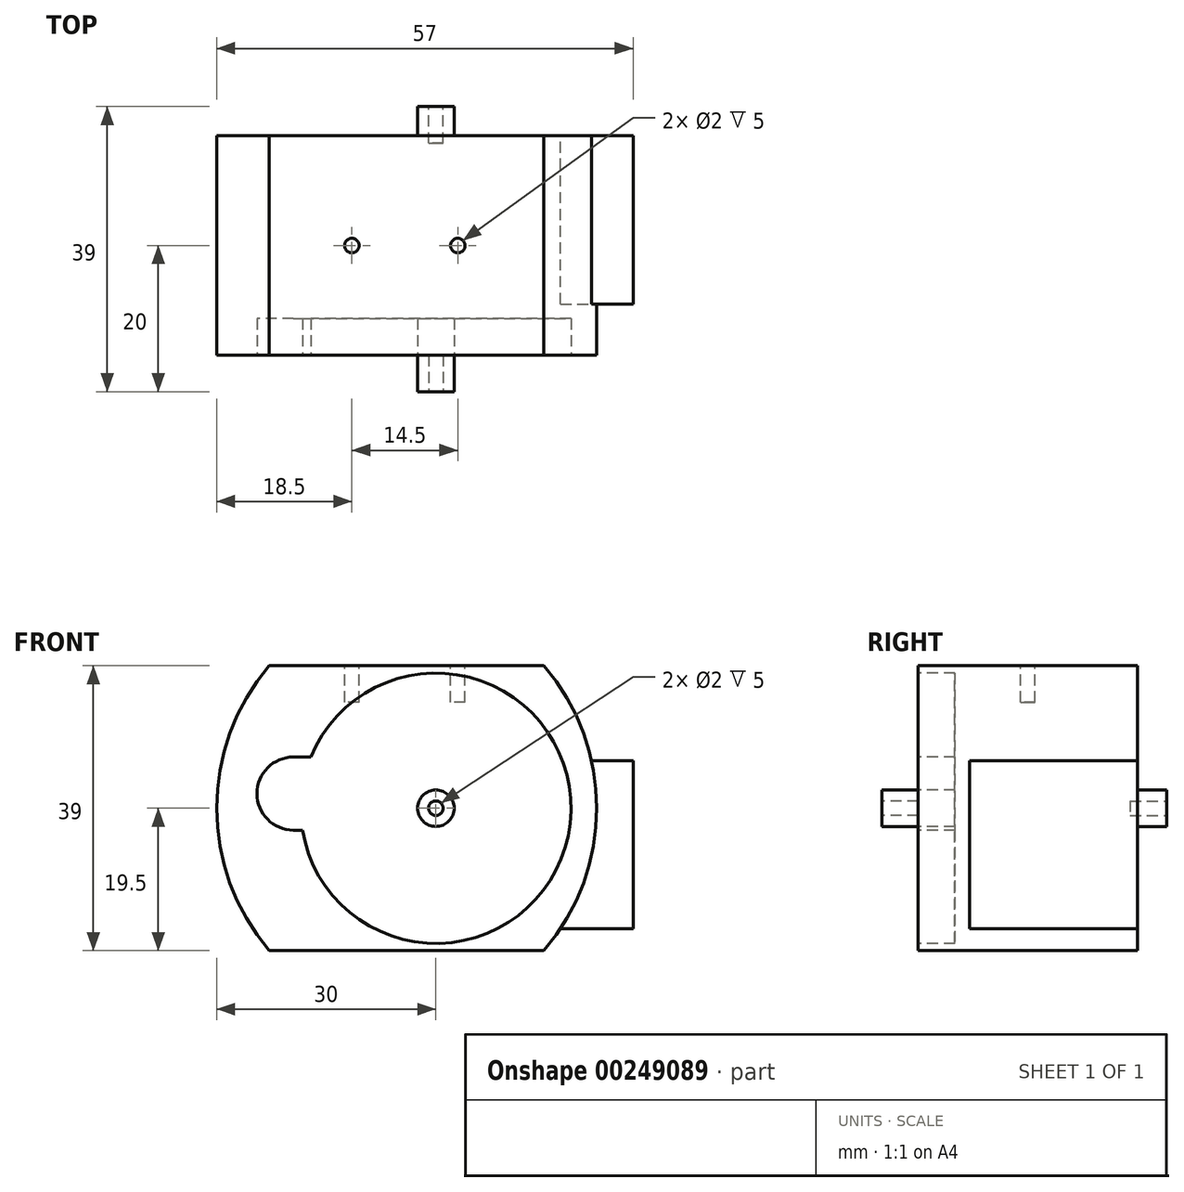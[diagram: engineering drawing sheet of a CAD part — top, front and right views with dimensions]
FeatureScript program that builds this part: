
annotation { "Feature Type Name" : "Feature", "Feature Type Description" : "" }
export const myFeature = defineFeature(function(context is Context, id is Id, definition is map)
    precondition{}
    {
        {
            var Q0;
            Q0=qCreatedBy(makeId("Front.planeOp"),FACE);
            var sketch = newSketch(context, id + "F0", { "sketchPlane" : qUnion([Q0])});
            skLineSegment(sketch, "E0.bottom", {"start": v(-22.8, 19.5) * mm, "end": v(14.8, 19.5) * mm});
            skLineSegment(sketch, "E0.top", {"start": v(-22.8, -19.5) * mm, "end": v(14.8, -19.5) * mm});
            skLineSegment(sketch, "E0.left", {"start": v(-30, 19.5) * mm, "end": v(-30, -19.5) * mm, "construction": true});
            skLineSegment(sketch, "E0.right", {"start": v(22, 19.5) * mm, "end": v(22, -19.5) * mm, "construction": true});
            skArc(sketch, "E1", {"start": v(-22.8, 19.5) * mm, "mid": v(-30, 0) * mm, "end": v(-22.8, -19.5) * mm});
            skArc(sketch, "E2", {"start": v(14.8, -19.5) * mm, "mid": v(22, 0) * mm, "end": v(14.8, 19.5) * mm});
            skCircle(sketch, "E3", {"center": v(0, 0) * mm, "radius": 18.5 * mm});
            skCircle(sketch, "E4", {"center": v(-19.5, 2) * mm, "radius": 5 * mm});
            skLineSegment(sketch, "E5", {"start": v(-19.5, 7) * mm, "end": v(-17.12, 7) * mm});
            skLineSegment(sketch, "E6", {"start": v(-19.5, -3) * mm, "end": v(-18.26, -3) * mm});
            skCircle(sketch, "E7", {"center": v(0, 0) * mm, "radius": 2.5 * mm});
            skCircle(sketch, "E8", {"center": v(-19.5, 2) * mm, "radius": 4.17 * mm, "construction": true});
            skCircle(sketch, "E9", {"center": v(-11.41, 0) * mm, "radius": 4.17 * mm, "construction": true});
            skSolve(sketch);
        }
        {
            var Q0;
            Q0=makeQuery(id+"F0.imprint","IMPRINT",FACE,{"disambiguationData":[TD([[makeQuery(id+"F0.imprint","IMPRINT",EDGE,{"derivedFrom":sQuery(id+"F0.wireOp",EDGE,"E0.bottom")}),-1.0]])]});
            var Q1;
            {var subQ0=sQuery(id+"F0.wireOp",EDGE,"E3");var subQ1=makeQuery(id+"F0.imprint","INTERSECT",VERTEX,{"derivedFrom":[subQ0,sQuery(id+"F0.wireOp",EDGE,"E5")]});Q1=makeQuery(id+"F0.imprint","IMPRINT",FACE,{"disambiguationData":[TD([[makeQuery(id+"F0.imprint","IMPRINT",EDGE,{"disambiguationData":[TD([[subQ1,-1.0]])],"derivedFrom":subQ0}),1.0]])]});}
            var Q2;
            {var subQ0=sQuery(id+"F0.wireOp",EDGE,"E4");var subQ1=sQuery(id+"F0.wireOp",EDGE,"E3");var subQ2=makeQuery(id+"F0.imprint","INTERSECT",VERTEX,{"disambiguationData":[OD(0.0)],"derivedFrom":[subQ1,subQ0]});Q2=makeQuery(id+"F0.imprint","IMPRINT",FACE,{"disambiguationData":[TD([[makeQuery(id+"F0.imprint","IMPRINT",EDGE,{"disambiguationData":[TD([[subQ2,-1.0]])],"derivedFrom":subQ1}),-1.0]])]});}
            var Q3;
            {var subQ0=sQuery(id+"F0.wireOp",EDGE,"E4");var subQ1=sQuery(id+"F0.wireOp",EDGE,"E3");var subQ2=makeQuery(id+"F0.imprint","INTERSECT",VERTEX,{"disambiguationData":[OD(0.0)],"derivedFrom":[subQ1,subQ0]});Q3=makeQuery(id+"F0.imprint","IMPRINT",FACE,{"disambiguationData":[TD([[makeQuery(id+"F0.imprint","IMPRINT",EDGE,{"disambiguationData":[TD([[subQ2,-1.0]])],"derivedFrom":subQ1}),1.0]])]});}
            var Q4;
            {var subQ0=sQuery(id+"F0.wireOp",EDGE,"E5");Q4=makeQuery(id+"F0.imprint","IMPRINT",FACE,{"disambiguationData":[TD([[makeQuery(id+"F0.imprint","IMPRINT",EDGE,{"derivedFrom":subQ0}),-1.0]])]});}
            var Q5;
            {var subQ0=sQuery(id+"F0.wireOp",EDGE,"E6");Q5=makeQuery(id+"F0.imprint","IMPRINT",FACE,{"disambiguationData":[TD([[makeQuery(id+"F0.imprint","IMPRINT",EDGE,{"derivedFrom":subQ0}),1.0]])]});}
            var Q6;
            Q6=makeQuery(id+"F0.imprint","IMPRINT",FACE,{"disambiguationData":[TD([[makeQuery(id+"F0.imprint","IMPRINT",EDGE,{"derivedFrom":sQuery(id+"F0.wireOp",EDGE,"E7")}),1.0]])]});
            extrude(context, id + "F1", {"entities" : qUnion([Q0, Q1, Q2, Q3, Q4, Q5, Q6]), "oppositeDirection" : true, "depth" : 30 * mm});
        }
        {
            var Q0;
            {var subQ0=sQuery(id+"F0.wireOp",EDGE,"E3");var subQ1=makeQuery(id+"F0.imprint","INTERSECT",VERTEX,{"derivedFrom":[subQ0,sQuery(id+"F0.wireOp",EDGE,"E5")]});Q0=makeQuery(id+"F0.imprint","IMPRINT",FACE,{"disambiguationData":[TD([[makeQuery(id+"F0.imprint","IMPRINT",EDGE,{"disambiguationData":[TD([[subQ1,-1.0]])],"derivedFrom":subQ0}),1.0]])]});}
            var Q1;
            {var subQ0=sQuery(id+"F0.wireOp",EDGE,"E5");Q1=makeQuery(id+"F0.imprint","IMPRINT",FACE,{"disambiguationData":[TD([[makeQuery(id+"F0.imprint","IMPRINT",EDGE,{"derivedFrom":subQ0}),-1.0]])]});}
            var Q2;
            {var subQ0=sQuery(id+"F0.wireOp",EDGE,"E6");Q2=makeQuery(id+"F0.imprint","IMPRINT",FACE,{"disambiguationData":[TD([[makeQuery(id+"F0.imprint","IMPRINT",EDGE,{"derivedFrom":subQ0}),1.0]])]});}
            var Q3;
            {var subQ0=sQuery(id+"F0.wireOp",EDGE,"E4");var subQ1=sQuery(id+"F0.wireOp",EDGE,"E3");var subQ2=makeQuery(id+"F0.imprint","INTERSECT",VERTEX,{"disambiguationData":[OD(0.0)],"derivedFrom":[subQ1,subQ0]});Q3=makeQuery(id+"F0.imprint","IMPRINT",FACE,{"disambiguationData":[TD([[makeQuery(id+"F0.imprint","IMPRINT",EDGE,{"disambiguationData":[TD([[subQ2,-1.0]])],"derivedFrom":subQ1}),-1.0]])]});}
            var Q4;
            {var subQ0=sQuery(id+"F0.wireOp",EDGE,"E4");var subQ1=sQuery(id+"F0.wireOp",EDGE,"E3");var subQ2=makeQuery(id+"F0.imprint","INTERSECT",VERTEX,{"disambiguationData":[OD(0.0)],"derivedFrom":[subQ1,subQ0]});Q4=makeQuery(id+"F0.imprint","IMPRINT",FACE,{"disambiguationData":[TD([[makeQuery(id+"F0.imprint","IMPRINT",EDGE,{"disambiguationData":[TD([[subQ2,-1.0]])],"derivedFrom":subQ1}),1.0]])]});}
            extrude(context, id + "F2", {"entities" : qUnion([Q0, Q1, Q2, Q3, Q4]), "operationType" : NewBodyOperationType.REMOVE, "oppositeDirection" : true, "depth" : 5 * mm});
        }
        {
            var Q0;
            Q0=makeQuery(id+"F0.imprint","IMPRINT",FACE,{"disambiguationData":[TD([[makeQuery(id+"F0.imprint","IMPRINT",EDGE,{"derivedFrom":sQuery(id+"F0.wireOp",EDGE,"E7")}),1.0]])]});
            extrude(context, id + "F3", {"entities" : qUnion([Q0]), "operationType" : NewBodyOperationType.ADD, "depth" : 5 * mm});
        }
        {
            var Q0;
            Q0=makeQuery(id+"F1.opExtrude","SWEPT_FACE",FACE,{"disambiguationData":[OSD([sQuery(id+"F0.wireOp",EDGE,"E0.bottom")])]});
            var sketch = newSketch(context, id + "F4", { "sketchPlane" : qUnion([Q0])});
            skPoint(sketch, "E10.0", {"position": v(-19.5, 0) * mm});
            skCircle(sketch, "E11", {"center": v(-11.5, 15) * mm, "radius": 1 * mm});
            skPoint(sketch, "E11.centerSnap0", {"position": v(-22.8, 15) * mm});
            skCircle(sketch, "E12", {"center": v(3, 15) * mm, "radius": 1 * mm});
            skSolve(sketch);
        }
        {
            var Q0;
            Q0 = qSketchRegion(id + "F4", true);
            extrude(context, id + "F5", {"entities" : qUnion([Q0]), "operationType" : NewBodyOperationType.REMOVE, "oppositeDirection" : true, "depth" : 5 * mm});
        }
        {
            var Q0;
            Q0=makeQuery(id+"F1.opExtrude","CAP_FACE",FACE,{"disambiguationData":[OSD([sQuery(id+"F0.wireOp",EDGE,"E0.bottom"),sQuery(id+"F0.wireOp",EDGE,"E0.top"),sQuery(id+"F0.wireOp",EDGE,"E1"),sQuery(id+"F0.wireOp",EDGE,"E2")])],"isStart":false});
            var sketch = newSketch(context, id + "F6", { "sketchPlane" : qUnion([Q0])});
            skLineSegment(sketch, "E13.bottom", {"start": v(0, -16.5) * mm, "end": v(-27, -16.5) * mm});
            skLineSegment(sketch, "E13.top", {"start": v(0, 6.5) * mm, "end": v(-27, 6.5) * mm});
            skLineSegment(sketch, "E13.left", {"start": v(0, -16.5) * mm, "end": v(0, 6.5) * mm});
            skLineSegment(sketch, "E13.right", {"start": v(-27, -16.5) * mm, "end": v(-27, 6.5) * mm});
            skCircle(sketch, "E14", {"center": v(0, 0) * mm, "radius": 2.5 * mm});
            skSolve(sketch);
        }
        {
            var Q0;
            {var subQ0=sQuery(id+"F6.wireOp",EDGE,"E13.right");Q0=makeQuery(id+"F6.imprint","IMPRINT",FACE,{"disambiguationData":[TD([[makeQuery(id+"F6.imprint","IMPRINT",EDGE,{"derivedFrom":subQ0}),-1.0]])]});}
            extrude(context, id + "F7", {"entities" : qUnion([Q0]), "operationType" : NewBodyOperationType.ADD, "oppositeDirection" : true, "depth" : 23 * mm});
        }
        {
            var Q0;
            {var subQ0=sQuery(id+"F6.wireOp",EDGE,"E14");var subQ1=sQuery(id+"F6.wireOp",EDGE,"E13.left");var subQ2=makeQuery(id+"F6.imprint","INTERSECT",VERTEX,{"disambiguationData":[OD(0.0)],"derivedFrom":[subQ1,subQ0]});Q0=makeQuery(id+"F6.imprint","IMPRINT",FACE,{"disambiguationData":[TD([[makeQuery(id+"F6.imprint","IMPRINT",EDGE,{"disambiguationData":[TD([[subQ2,-1.0]])],"derivedFrom":subQ1}),1.0]])]});}
            var Q1;
            {var subQ0=sQuery(id+"F6.wireOp",EDGE,"E14");var subQ1=sQuery(id+"F6.wireOp",EDGE,"E13.left");var subQ2=makeQuery(id+"F6.imprint","INTERSECT",VERTEX,{"disambiguationData":[OD(0.0)],"derivedFrom":[subQ1,subQ0]});Q1=makeQuery(id+"F6.imprint","IMPRINT",FACE,{"disambiguationData":[TD([[makeQuery(id+"F6.imprint","IMPRINT",EDGE,{"disambiguationData":[TD([[subQ2,-1.0]])],"derivedFrom":subQ1}),-1.0]])]});}
            extrude(context, id + "F8", {"entities" : qUnion([Q0, Q1]), "operationType" : NewBodyOperationType.ADD, "depth" : 4 * mm});
        }
        {
            var Q0;
            Q0=makeQuery(id+"F3.opExtrude","CAP_FACE",FACE,{"disambiguationData":[OSD([sQuery(id+"F0.wireOp",EDGE,"E7")])],"isStart":false});
            var sketch = newSketch(context, id + "F9", { "sketchPlane" : qUnion([Q0])});
            skCircle(sketch, "E15", {"center": v(0, 0) * mm, "radius": 1 * mm});
            skSolve(sketch);
        }
        {
            var Q0;
            Q0 = qSketchRegion(id + "F9", true);
            extrude(context, id + "F10", {"entities" : qUnion([Q0]), "operationType" : NewBodyOperationType.REMOVE, "oppositeDirection" : true, "depth" : 5 * mm});
        }
        {
            var Q0;
            Q0=makeQuery(id+"F8.opExtrude","CAP_FACE",FACE,{"disambiguationData":[OSD([sQuery(id+"F6.wireOp",EDGE,"E14")])],"isStart":false});
            var sketch = newSketch(context, id + "F11", { "sketchPlane" : qUnion([Q0])});
            skCircle(sketch, "E16", {"center": v(0, 0) * mm, "radius": 1 * mm});
            skSolve(sketch);
        }
        {
            var Q0;
            Q0 = qSketchRegion(id + "F11", true);
            extrude(context, id + "F12", {"entities" : qUnion([Q0]), "operationType" : NewBodyOperationType.REMOVE, "oppositeDirection" : true, "depth" : 5 * mm});
        }
    });
